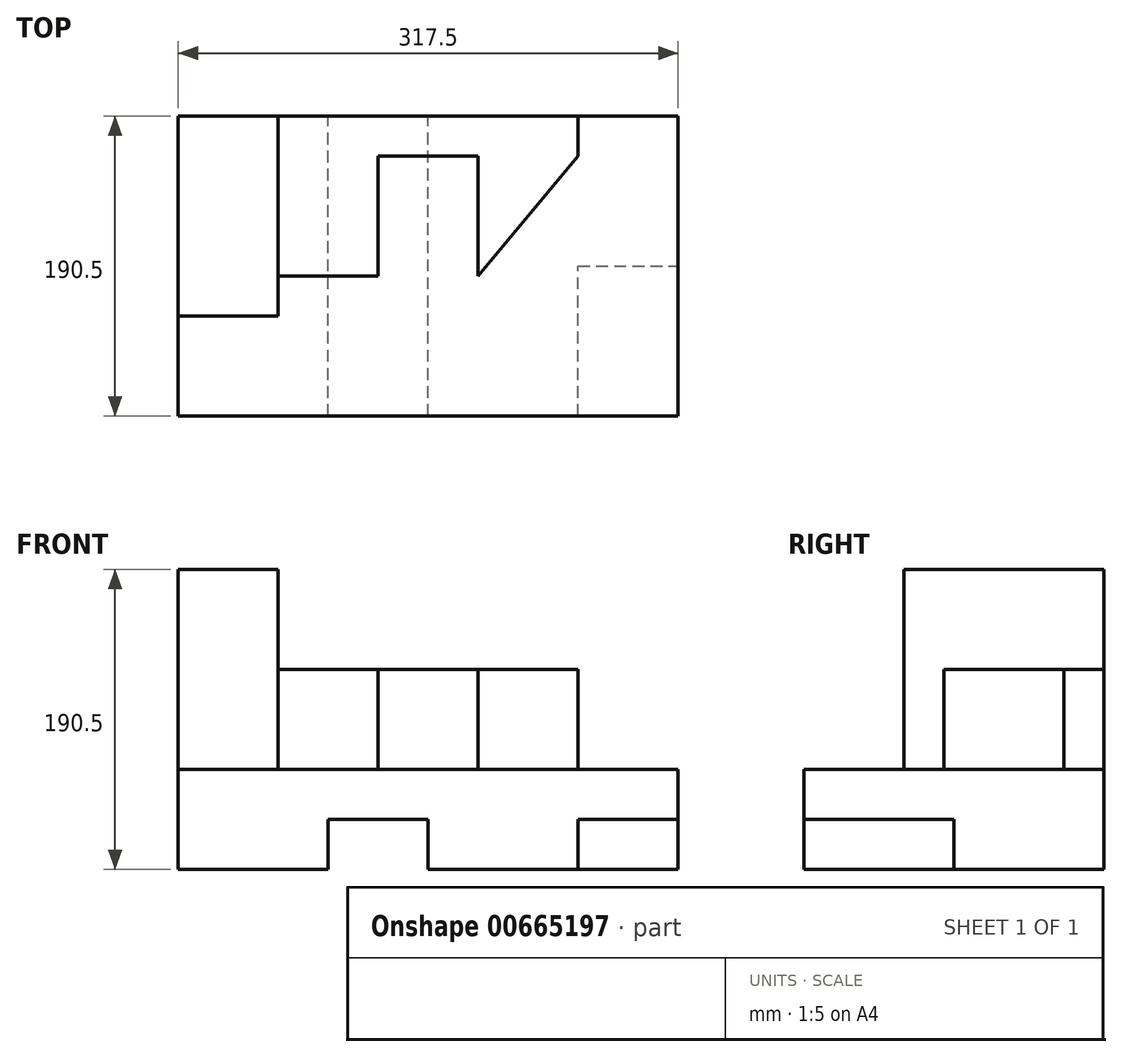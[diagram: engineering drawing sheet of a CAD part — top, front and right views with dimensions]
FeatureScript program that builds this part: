
annotation { "Feature Type Name" : "Feature", "Feature Type Description" : "" }
export const myFeature = defineFeature(function(context is Context, id is Id, definition is map)
    precondition{}
    {
        {
            var Q0;
            Q0=qCreatedBy(makeId("Top.planeOp"),FACE);
            var sketch = newSketch(context, id + "F0", { "sketchPlane" : qUnion([Q0])});
            skLineSegment(sketch, "E0", {"start": v(0, 0) * mm, "end": v(190.5, 0) * mm});
            skLineSegment(sketch, "E1", {"start": v(190.5, 0) * mm, "end": v(190.5, 317.5) * mm});
            skLineSegment(sketch, "E2", {"start": v(190.5, 317.5) * mm, "end": v(0, 317.5) * mm});
            skLineSegment(sketch, "E3", {"start": v(0, 317.5) * mm, "end": v(0, 0) * mm});
            skSolve(sketch);
        }
        {
            var Q0;
            Q0=makeQuery(id+"F0.imprint","IMPRINT",FACE,{"disambiguationData":[TD([[makeQuery(id+"F0.imprint","IMPRINT",EDGE,{"derivedFrom":sQuery(id+"F0.wireOp",EDGE,"E0")}),1.0]])]});
            extrude(context, id + "F1", {"entities" : qUnion([Q0]), "endBound" : BoundingType.SYMMETRIC, "depth" : 31.75 * mm, "offsetDistance" : 25.4 * mm});
        }
        {
            var Q0;
            Q0=makeQuery(id+"F1.opExtrude","CAP_FACE",FACE,{"disambiguationData":[OSD([sQuery(id+"F0.wireOp",EDGE,"E0"),sQuery(id+"F0.wireOp",EDGE,"E1"),sQuery(id+"F0.wireOp",EDGE,"E2"),sQuery(id+"F0.wireOp",EDGE,"E3")])],"isStart":false});
            var sketch = newSketch(context, id + "F2", { "sketchPlane" : qUnion([Q0])});
            skLineSegment(sketch, "E4", {"start": v(0, 63.5) * mm, "end": v(127, 63.5) * mm});
            skLineSegment(sketch, "E5", {"start": v(127, 63.5) * mm, "end": v(127, 0) * mm});
            skLineSegment(sketch, "E6", {"start": v(25.4, 127) * mm, "end": v(101.6, 127) * mm});
            skLineSegment(sketch, "E7", {"start": v(101.6, 127) * mm, "end": v(101.6, 63.5) * mm});
            skLineSegment(sketch, "E8", {"start": v(25.4, 190.5) * mm, "end": v(25.4, 127) * mm});
            skLineSegment(sketch, "E9", {"start": v(25.4, 190.5) * mm, "end": v(101.6, 190.5) * mm});
            skLineSegment(sketch, "E10", {"start": v(0, 254) * mm, "end": v(25.4, 254) * mm});
            skLineSegment(sketch, "E11", {"start": v(101.6, 190.5) * mm, "end": v(25.4, 254) * mm});
            skSolve(sketch);
        }
        {
            var Q0;
            {var subQ0=sQuery(id+"F2.wireOp",EDGE,"E5");Q0=makeQuery(id+"F2.imprint","IMPRINT",FACE,{"disambiguationData":[TD([[makeQuery(id+"F2.imprint","IMPRINT",EDGE,{"derivedFrom":subQ0}),-1.0]])]});}
            extrude(context, id + "F3", {"entities" : qUnion([Q0]), "operationType" : NewBodyOperationType.ADD, "depth" : 127 * mm, "offsetDistance" : 25.4 * mm});
        }
        {
            var Q0;
            Q0=makeQuery(id+"F2.imprint","IMPRINT",FACE,{"disambiguationData":[TD([[makeQuery(id+"F2.imprint","IMPRINT",EDGE,{"derivedFrom":sQuery(id+"F2.wireOp",EDGE,"E6")}),-1.0]])]});
            extrude(context, id + "F4", {"entities" : qUnion([Q0]), "operationType" : NewBodyOperationType.ADD, "depth" : 63.5 * mm, "offsetDistance" : 25.4 * mm});
        }
        {
            var Q0;
            Q0=makeQuery(id+"F1.opExtrude","CAP_FACE",FACE,{"disambiguationData":[OSD([sQuery(id+"F0.wireOp",EDGE,"E0"),sQuery(id+"F0.wireOp",EDGE,"E1"),sQuery(id+"F0.wireOp",EDGE,"E2"),sQuery(id+"F0.wireOp",EDGE,"E3")])],"isStart":true});
            var sketch = newSketch(context, id + "F5", { "sketchPlane" : qUnion([Q0])});
            skLineSegment(sketch, "E12", {"start": v(190.5, -95.25) * mm, "end": v(0, -95.25) * mm});
            skLineSegment(sketch, "E13", {"start": v(190.5, -158.75) * mm, "end": v(0, -158.75) * mm});
            skLineSegment(sketch, "E14", {"start": v(190.5, -254) * mm, "end": v(95.25, -254) * mm});
            skLineSegment(sketch, "E15", {"start": v(95.25, -254) * mm, "end": v(95.25, -317.5) * mm});
            skSolve(sketch);
        }
        {
            var Q0;
            {var subQ0=sQuery(id+"F5.wireOp",EDGE,"E12");Q0=makeQuery(id+"F5.imprint","IMPRINT",FACE,{"disambiguationData":[TD([[makeQuery(id+"F5.imprint","IMPRINT",EDGE,{"derivedFrom":subQ0}),-1.0]])]});}
            var Q1;
            {var subQ0=sQuery(id+"F5.wireOp",EDGE,"E13");Q1=makeQuery(id+"F5.imprint","IMPRINT",FACE,{"disambiguationData":[TD([[makeQuery(id+"F5.imprint","IMPRINT",EDGE,{"derivedFrom":subQ0}),1.0]])]});}
            extrude(context, id + "F6", {"entities" : qUnion([Q0, Q1]), "operationType" : NewBodyOperationType.ADD, "depth" : 31.75 * mm, "offsetDistance" : 25.4 * mm});
        }
        {
            var Q0;
            Q0=makeQuery(id+"F1.opExtrude","SWEPT_BODY",BODY,{"disambiguationData":[OSD([sQuery(id+"F0.wireOp",EDGE,"E0"),sQuery(id+"F0.wireOp",EDGE,"E1"),sQuery(id+"F0.wireOp",EDGE,"E2"),sQuery(id+"F0.wireOp",EDGE,"E3")])]});
            var Q1;
            {var subQ0=sQuery(id+"F0.wireOp",EDGE,"E3");var subQ1=sQuery(id+"F0.wireOp",EDGE,"E0");Q1=makeQuery(id+"F6.boolean.opBoolean","MERGE",EDGE,{"derivedFrom":[makeQuery(id+"F3.boolean.opBoolean","MERGE",EDGE,{"derivedFrom":[makeQuery(id+"F1.opExtrude","SWEPT_EDGE",EDGE,{"disambiguationData":[OSD([subQ1,subQ0])]}),makeQuery(id+"F3.opExtrude","SWEPT_EDGE",EDGE,{"disambiguationData":[OSD([subQ1,subQ0])]})]}),makeQuery(id+"F6.opExtrude","SWEPT_EDGE",EDGE,{"disambiguationData":[OSD([subQ1,subQ0])]})]});}
            transform(context, id + "F7", {"entities" : qUnion([Q0]), "transformType" : TransformType.ROTATION, "transformAxis" : qUnion([Q1]), "angle" : 90 * degree, "makeCopy" : false});
        }
    });
